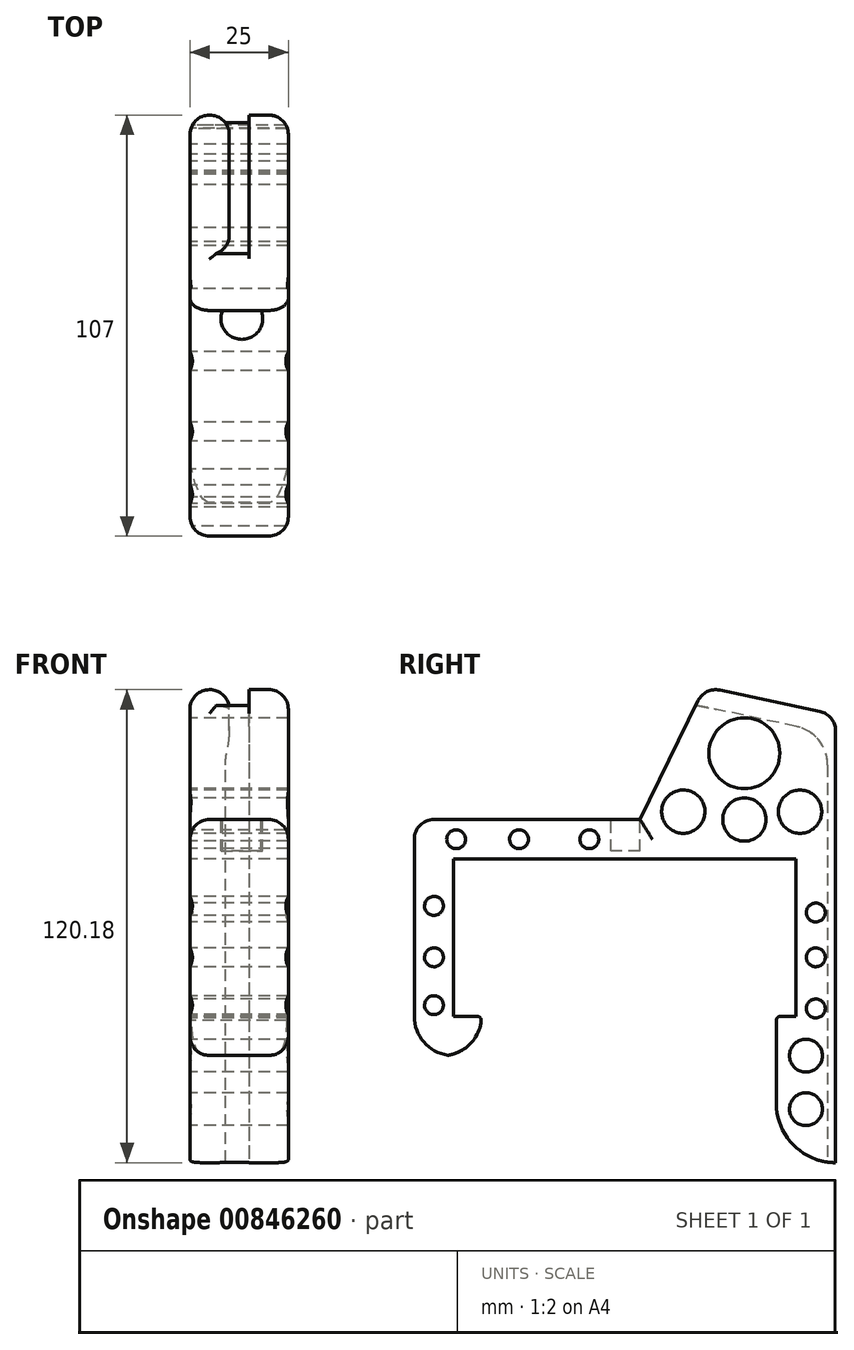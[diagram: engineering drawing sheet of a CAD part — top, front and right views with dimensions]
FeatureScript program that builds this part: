
annotation { "Feature Type Name" : "Feature", "Feature Type Description" : "" }
export const myFeature = defineFeature(function(context is Context, id is Id, definition is map)
    precondition{}
    {
        {
            var Q0;
            Q0=qCreatedBy(makeId("Right.planeOp"),FACE);
            var sketch = newSketch(context, id + "F0", { "sketchPlane" : qUnion([Q0])});
            skLineSegment(sketch, "E0.bottom", {"start": v(-21.63, 40) * mm, "end": v(65.37, 40) * mm, "construction": true});
            skLineSegment(sketch, "E0.top", {"start": v(-21.63, 0) * mm, "end": v(65.37, 0) * mm, "construction": true});
            skLineSegment(sketch, "E0.left", {"start": v(-21.63, 40) * mm, "end": v(-21.63, 0) * mm, "construction": true});
            skLineSegment(sketch, "E0.right", {"start": v(65.37, 40) * mm, "end": v(65.37, 0) * mm, "construction": true});
            skLineSegment(sketch, "E1.bottom", {"start": v(-31.63, 40) * mm, "end": v(75.37, 40) * mm});
            skLineSegment(sketch, "E1.top", {"start": v(-31.63, 50) * mm, "end": v(75.37, 50) * mm});
            skLineSegment(sketch, "E1.left", {"start": v(-31.63, 40) * mm, "end": v(-31.63, 50) * mm});
            skLineSegment(sketch, "E1.right", {"start": v(75.37, 40) * mm, "end": v(75.37, 50) * mm});
            skLineSegment(sketch, "E2.bottom", {"start": v(-31.63, 40) * mm, "end": v(-21.63, 40) * mm});
            skLineSegment(sketch, "E2.top", {"start": v(-31.63, 40) * mm, "end": v(-21.63, 40) * mm});
            skLineSegment(sketch, "E2.left", {"start": v(-31.63, 40) * mm, "end": v(-31.63, 40) * mm});
            skLineSegment(sketch, "E2.right", {"start": v(-21.63, 40) * mm, "end": v(-21.63, 40) * mm});
            skLineSegment(sketch, "E3.bottom", {"start": v(-21.63, 40) * mm, "end": v(-31.63, 40) * mm});
            skLineSegment(sketch, "E3.top", {"start": v(-21.63, -10) * mm, "end": v(-31.63, -10) * mm});
            skLineSegment(sketch, "E3.left", {"start": v(-21.63, 40) * mm, "end": v(-21.63, -10) * mm});
            skLineSegment(sketch, "E3.right", {"start": v(-31.63, 40) * mm, "end": v(-31.63, -10) * mm});
            skLineSegment(sketch, "E4.bottom", {"start": v(75.37, 40) * mm, "end": v(65.37, 40) * mm});
            skLineSegment(sketch, "E4.top", {"start": v(75.37, -10) * mm, "end": v(65.37, -10) * mm});
            skLineSegment(sketch, "E4.left", {"start": v(75.37, 40) * mm, "end": v(75.37, -10) * mm});
            skLineSegment(sketch, "E4.right", {"start": v(65.37, 40) * mm, "end": v(65.37, -10) * mm});
            skLineSegment(sketch, "E5.bottom", {"start": v(-21.63, -10) * mm, "end": v(-14.63, -10) * mm});
            skLineSegment(sketch, "E5.top", {"start": v(-21.63, 0) * mm, "end": v(-15.63, 0) * mm});
            skLineSegment(sketch, "E5.left", {"start": v(-21.63, -10) * mm, "end": v(-21.63, 0) * mm});
            skLineSegment(sketch, "E5.right", {"start": v(-14.63, -10) * mm, "end": v(-14.63, -1) * mm});
            skLineSegment(sketch, "E6.bottom", {"start": v(65.37, -10) * mm, "end": v(60.37, -10) * mm});
            skLineSegment(sketch, "E6.top", {"start": v(65.37, 0) * mm, "end": v(61.37, 0) * mm});
            skLineSegment(sketch, "E6.left", {"start": v(65.37, -10) * mm, "end": v(65.37, 0) * mm});
            skLineSegment(sketch, "E6.right", {"start": v(60.37, -10) * mm, "end": v(60.37, -1) * mm});
            skPoint(sketch, "E7.visualSharp", {"position": v(-14.63, 0) * mm});
            skArc(sketch, "E7.filletArc", {"start": v(-14.63, -1) * mm, "mid": v(-14.93, -0.3) * mm, "end": v(-15.63, 0) * mm});
            skPoint(sketch, "E8.visualSharp", {"position": v(60.37, 0) * mm});
            skArc(sketch, "E8.filletArc", {"start": v(61.37, 0) * mm, "mid": v(60.66, -0.3) * mm, "end": v(60.37, -1) * mm});
            skLineSegment(sketch, "E9.left", {"start": v(75.37, -10) * mm, "end": v(75.37, 0) * mm});
            skLineSegment(sketch, "E10.bottom", {"start": v(75.37, 50) * mm, "end": v(25.72, 50) * mm});
            skLineSegment(sketch, "E10.right", {"start": v(25.72, 50) * mm, "end": v(40.44, 80.2) * mm});
            skLineSegment(sketch, "E11.bottom", {"start": v(60.37, -10) * mm, "end": v(75.37, -10) * mm});
            skLineSegment(sketch, "E11.top", {"start": v(60.37, -37.18) * mm, "end": v(75.37, -37.18) * mm});
            skLineSegment(sketch, "E11.left", {"start": v(60.37, -10) * mm, "end": v(60.37, -37.18) * mm});
            skLineSegment(sketch, "E11.right", {"start": v(75.37, -10) * mm, "end": v(75.37, -37.18) * mm});
            skLineSegment(sketch, "E12", {"start": v(45.98, 82.9) * mm, "end": v(71.4, 77.49) * mm});
            skLineSegment(sketch, "E13", {"start": v(75.37, 72.6) * mm, "end": v(75.37, 50) * mm});
            skPoint(sketch, "E14.positionSnap0", {"position": v(58.76, 80.17) * mm});
            skPoint(sketch, "E14.positionSnap1", {"position": v(33.93, 66.85) * mm});
            skPoint(sketch, "E15", {"position": v(67.87, -23.6) * mm});
            skPoint(sketch, "E15.positionSnap0", {"position": v(75.37, -23.6) * mm});
            skPoint(sketch, "E15.positionSnap1", {"position": v(67.87, -10) * mm});
            skCircle(sketch, "E16", {"center": v(67.87, -23.6) * mm, "radius": 4.18 * mm});
            skPoint(sketch, "E17", {"position": v(70.37, 15) * mm});
            skPoint(sketch, "E17.positionSnap0", {"position": v(70.37, -10) * mm});
            skPoint(sketch, "E17.positionSnap1", {"position": v(65.37, 15) * mm});
            skPoint(sketch, "E18", {"position": v(-26.63, 15) * mm});
            skPoint(sketch, "E18.positionSnap0", {"position": v(-26.63, -10) * mm});
            skPoint(sketch, "E18.positionSnap1", {"position": v(-31.63, 15) * mm});
            skPoint(sketch, "E19", {"position": v(-26.63, 2.84) * mm});
            skPoint(sketch, "E20", {"position": v(-26.63, 28.06) * mm});
            skPoint(sketch, "E21", {"position": v(70.37, 2) * mm});
            skPoint(sketch, "E22", {"position": v(70.37, 26.38) * mm});
            skPoint(sketch, "E23", {"position": v(37.84, 45) * mm});
            skPoint(sketch, "E23.positionSnap0", {"position": v(75.37, 45) * mm});
            skPoint(sketch, "E24", {"position": v(12.84, 45) * mm});
            skPoint(sketch, "E25", {"position": v(-5.03, 45) * mm});
            skPoint(sketch, "E26", {"position": v(-21, 45) * mm});
            skCircle(sketch, "E27", {"center": v(70.37, 15) * mm, "radius": 2.4 * mm});
            skCircle(sketch, "E28", {"center": v(70.37, 2) * mm, "radius": 2.4 * mm});
            skCircle(sketch, "E29", {"center": v(70.37, 26.38) * mm, "radius": 2.4 * mm});
            skCircle(sketch, "E30", {"center": v(-26.63, 2.84) * mm, "radius": 2.4 * mm});
            skCircle(sketch, "E31", {"center": v(-26.63, 15) * mm, "radius": 2.4 * mm});
            skCircle(sketch, "E32", {"center": v(-26.63, 28.06) * mm, "radius": 2.4 * mm});
            skCircle(sketch, "E33", {"center": v(12.84, 45) * mm, "radius": 2.4 * mm});
            skCircle(sketch, "E34", {"center": v(-5.03, 45) * mm, "radius": 2.4 * mm});
            skCircle(sketch, "E35", {"center": v(-21, 45) * mm, "radius": 2.4 * mm});
            skCircle(sketch, "E36", {"center": v(67.87, -10) * mm, "radius": 4.18 * mm});
            skPoint(sketch, "E37", {"position": v(36.7, 52) * mm});
            skPoint(sketch, "E38", {"position": v(66.37, 52) * mm});
            skCircle(sketch, "E39", {"center": v(36.7, 52) * mm, "radius": 5.5 * mm});
            skCircle(sketch, "E40", {"center": v(66.37, 52) * mm, "radius": 5.5 * mm});
            skPoint(sketch, "E41.visualSharp", {"position": v(42.15, 83.7) * mm});
            skArc(sketch, "E41.filletArc", {"start": v(45.98, 82.9) * mm, "mid": v(42.74, 82.5) * mm, "end": v(40.44, 80.2) * mm});
            skPoint(sketch, "E42.visualSharp", {"position": v(75.37, 76.64) * mm});
            skArc(sketch, "E42.filletArc", {"start": v(75.37, 72.6) * mm, "mid": v(74.25, 75.74) * mm, "end": v(71.4, 77.49) * mm});
            skCircle(sketch, "E43", {"center": v(52.23, 66.85) * mm, "radius": 9 * mm});
            skCircle(sketch, "E44", {"center": v(52.23, 50) * mm, "radius": 5.5 * mm});
            skSolve(sketch);
        }
        {
            var Q0;
            Q0 = qSketchRegion(id + "F0", true);
            extrude(context, id + "F1", {"entities" : qUnion([Q0]), "depth" : 25 * mm, "offsetDistance" : 25 * mm});
        }
        {
            var Q0;
            Q0=makeQuery(id+"F1.opExtrude","SWEPT_EDGE",EDGE,{"disambiguationData":[OSD([sQuery(id+"F0.wireOp",EDGE,"E11.top"),sQuery(id+"F0.wireOp",EDGE,"E11.left")])]});
            fillet(context, id + "F2", {"entities" : qUnion([Q0]), "radius" : 15 * mm, "tangentPropagation" : true, "allowEdgeOverflow" : false});
        }
        {
            var Q0;
            Q0=makeQuery(id+"F1.opExtrude","SWEPT_EDGE",EDGE,{"disambiguationData":[OSD([sQuery(id+"F0.wireOp",EDGE,"E5.bottom"),sQuery(id+"F0.wireOp",EDGE,"E5.right")])]});
            var Q1;
            Q1=makeQuery(id+"F1.opExtrude","SWEPT_EDGE",EDGE,{"disambiguationData":[OSD([sQuery(id+"F0.wireOp",EDGE,"E3.top"),sQuery(id+"F0.wireOp",EDGE,"E3.right")])]});
            fillet(context, id + "F3", {"entities" : qUnion([Q0, Q1]), "radius" : 10 * mm, "tangentPropagation" : true, "allowEdgeOverflow" : false});
        }
        {
            var Q0;
            Q0=makeQuery(id+"F1.opExtrude","SWEPT_FACE",FACE,{"disambiguationData":[OSD([sQuery(id+"F0.wireOp",EDGE,"E12")])]});
            var sketch = newSketch(context, id + "F4", { "sketchPlane" : qUnion([Q0])});
            skLineSegment(sketch, "E45.bottom", {"start": v(10, 58.63) * mm, "end": v(15, 58.63) * mm});
            skLineSegment(sketch, "E45.top", {"start": v(10, 22.88) * mm, "end": v(15, 22.88) * mm});
            skLineSegment(sketch, "E45.left", {"start": v(10, 58.63) * mm, "end": v(10, 22.88) * mm});
            skLineSegment(sketch, "E45.right", {"start": v(15, 58.63) * mm, "end": v(15, 22.88) * mm});
            skSolve(sketch);
        }
        {
            var Q0;
            {var subQ0=sQuery(id+"F4.wireOp",EDGE,"E45.bottom");Q0=makeQuery(id+"F4.imprint","IMPRINT",FACE,{"disambiguationData":[TD([[makeQuery(id+"F4.imprint","IMPRINT",EDGE,{"derivedFrom":subQ0}),-1.0]])]});}
            var Q1;
            {var subQ0=sQuery(id+"F4.wireOp",EDGE,"E45.left");var subQ1=sQuery(id+"F0.wireOp",EDGE,"E12");var subQ2=makeQuery(id+"F1.opExtrude","SWEPT_EDGE",EDGE,{"disambiguationData":[OSD([subQ1,sQuery(id+"F0.wireOp",EDGE,"E42.filletArc")])]});var subQ3=makeQuery(id+"F4.imprint","INTERSECT",VERTEX,{"derivedFrom":[subQ2,subQ0]});Q1=makeQuery(id+"F4.imprint","IMPRINT",FACE,{"disambiguationData":[TD([[makeQuery(id+"F4.imprint","IMPRINT",EDGE,{"disambiguationData":[TD([[subQ3,-1.0]])],"derivedFrom":subQ0}),1.0]])]});}
            var Q2;
            {var subQ0=sQuery(id+"F4.wireOp",EDGE,"E45.top");Q2=makeQuery(id+"F4.imprint","IMPRINT",FACE,{"disambiguationData":[TD([[makeQuery(id+"F4.imprint","IMPRINT",EDGE,{"derivedFrom":subQ0}),1.0]])]});}
            extrude(context, id + "F5", {"entities" : qUnion([Q0, Q1, Q2]), "operationType" : NewBodyOperationType.REMOVE, "oppositeDirection" : true, "depth" : 5 * mm, "offsetDistance" : 25 * mm});
        }
        {
            var Q0;
            Q0=makeQuery(id+"F1.opExtrude","SWEPT_FACE",FACE,{"disambiguationData":[OSD([sQuery(id+"F0.wireOp",EDGE,"E1.right"),sQuery(id+"F0.wireOp",EDGE,"E4.left"),sQuery(id+"F0.wireOp",EDGE,"E9.left"),sQuery(id+"F0.wireOp",EDGE,"E11.right"),sQuery(id+"F0.wireOp",EDGE,"E13")])]});
            var sketch = newSketch(context, id + "F6", { "sketchPlane" : qUnion([Q0])});
            skLineSegment(sketch, "E46.bottom", {"start": v(-15, 72.6) * mm, "end": v(-10, 72.6) * mm});
            skLineSegment(sketch, "E46.top", {"start": v(-15, -37.18) * mm, "end": v(-10, -37.18) * mm});
            skLineSegment(sketch, "E46.left", {"start": v(-15, 72.6) * mm, "end": v(-15, -37.18) * mm});
            skLineSegment(sketch, "E46.right", {"start": v(-10, 72.6) * mm, "end": v(-10, -37.18) * mm});
            skSolve(sketch);
        }
        {
            var Q0;
            Q0 = qSketchRegion(id + "F6", true);
            extrude(context, id + "F7", {"entities" : qUnion([Q0]), "operationType" : NewBodyOperationType.REMOVE, "oppositeDirection" : true, "depth" : 2 * mm, "offsetDistance" : 25 * mm});
        }
        {
            var Q0;
            {var subQ0=sQuery(id+"F4.wireOp",EDGE,"E45.bottom");var subQ1=sQuery(id+"F4.wireOp",EDGE,"E45.right");var subQ2=sQuery(id+"F4.wireOp",EDGE,"E45.left");Q0=makeQuery(id+"F7.boolean.opBoolean","INTERSECT",EDGE,{"derivedFrom":[makeQuery(id+"F5.boolean.opBoolean","COPY",FACE,{"disambiguationData":[TD([makeQuery(id+"F5.opExtrude","SWEPT_FACE",FACE,{"disambiguationData":[OSD([subQ0])]})])],"derivedFrom":makeQuery(id+"F5.opExtrude","CAP_FACE",FACE,{"disambiguationData":[OSD([subQ0,sQuery(id+"F4.wireOp",EDGE,"E45.top"),subQ2,subQ1])],"isStart":false})}),makeQuery(id+"F7.opExtrude","CAP_FACE",FACE,{"disambiguationData":[OSD([sQuery(id+"F6.wireOp",EDGE,"E46.bottom"),sQuery(id+"F6.wireOp",EDGE,"E46.top"),sQuery(id+"F6.wireOp",EDGE,"E46.left"),sQuery(id+"F6.wireOp",EDGE,"E46.right")])],"isStart":false})]});}
            var Q1;
            {var subQ0=sQuery(id+"F0.wireOp",EDGE,"E10.right");Q1=makeQuery(id+"F5.boolean.opBoolean","SPLIT",EDGE,{"disambiguationData":[topologyDisambiguationEdgeConnected([makeQuery(id+"F1.opExtrude","SWEPT_FACE",FACE,{"disambiguationData":[OSD([subQ0])]}),makeQuery(id+"F5.opExtrude","SWEPT_FACE",FACE,{"disambiguationData":[OSD([sQuery(id+"F4.wireOp",EDGE,"E45.top")])]})])],"derivedFrom":makeQuery(id+"F1.opExtrude","SWEPT_EDGE",EDGE,{"disambiguationData":[OSD([subQ0,sQuery(id+"F0.wireOp",EDGE,"E41.filletArc")])]})});}
            fillet(context, id + "F8", {"entities" : qUnion([Q0, Q1]), "radius" : 10 * mm, "tangentPropagation" : true, "allowEdgeOverflow" : false});
        }
        {
            var Q0;
            Q0=makeQuery(id+"F7.boolean.opBoolean","COPY",EDGE,{"derivedFrom":makeQuery(id+"F7.opExtrude","CAP_EDGE",EDGE,{"disambiguationData":[OSD([sQuery(id+"F6.wireOp",EDGE,"E46.left")])],"isStart":true})});
            var Q1;
            Q1=makeQuery(id+"F7.boolean.opBoolean","COPY",EDGE,{"derivedFrom":makeQuery(id+"F7.opExtrude","CAP_EDGE",EDGE,{"disambiguationData":[OSD([sQuery(id+"F6.wireOp",EDGE,"E46.right")])],"isStart":true})});
            fillet(context, id + "F9", {"entities" : qUnion([Q0, Q1]), "radius" : 5 * mm, "tangentPropagation" : true, "allowEdgeOverflow" : false});
        }
        {
            var Q0;
            Q0=makeQuery(id+"F1.opExtrude","CAP_EDGE",EDGE,{"disambiguationData":[OSD([sQuery(id+"F0.wireOp",EDGE,"E10.right")])],"isStart":false});
            var Q1;
            Q1=makeQuery(id+"F1.opExtrude","CAP_EDGE",EDGE,{"disambiguationData":[OSD([sQuery(id+"F0.wireOp",EDGE,"E10.right")])],"isStart":true});
            var Q2;
            Q2=makeQuery(id+"F1.opExtrude","CAP_EDGE",EDGE,{"disambiguationData":[OSD([sQuery(id+"F0.wireOp",EDGE,"E1.top")])],"isStart":false});
            var Q3;
            Q3=makeQuery(id+"F1.opExtrude","CAP_EDGE",EDGE,{"disambiguationData":[OSD([sQuery(id+"F0.wireOp",EDGE,"E1.top")])],"isStart":true});
            var Q4;
            Q4=makeQuery(id+"F1.opExtrude","SWEPT_EDGE",EDGE,{"disambiguationData":[OSD([sQuery(id+"F0.wireOp",EDGE,"E1.top"),sQuery(id+"F0.wireOp",EDGE,"E1.left")])]});
            var Q5;
            Q5=makeQuery(id+"F1.opExtrude","CAP_EDGE",EDGE,{"disambiguationData":[OSD([sQuery(id+"F0.wireOp",EDGE,"E1.left"),sQuery(id+"F0.wireOp",EDGE,"E3.right")])],"isStart":false});
            var Q6;
            Q6=makeQuery(id+"F1.opExtrude","CAP_EDGE",EDGE,{"disambiguationData":[OSD([sQuery(id+"F0.wireOp",EDGE,"E1.left"),sQuery(id+"F0.wireOp",EDGE,"E3.right")])],"isStart":true});
            fillet(context, id + "F10", {"entities" : qUnion([Q0, Q1, Q2, Q3, Q4, Q5, Q6]), "radius" : 5 * mm, "tangentPropagation" : true, "allowEdgeOverflow" : false});
        }
        {
            var Q0;
            Q0=makeQuery(id+"F1.opExtrude","SWEPT_FACE",FACE,{"disambiguationData":[OSD([sQuery(id+"F0.wireOp",EDGE,"E1.top")])]});
            var sketch = newSketch(context, id + "F11", { "sketchPlane" : qUnion([Q0])});
            skArc(sketch, "E47", {"start": v(8.27, 25.72) * mm, "mid": v(13.19, 18.36) * mm, "end": v(18.1, 25.72) * mm});
            skSolve(sketch);
        }
        {
            var Q0;
            Q0 = qSketchRegion(id + "F11", true);
            var Q1;
            {var subQ0=sQuery(id+"F11.wireOp",EDGE,"E47");Q1=makeQuery(id+"F11.imprint","IMPRINT",FACE,{"disambiguationData":[TD([[makeQuery(id+"F11.imprint","IMPRINT",EDGE,{"derivedFrom":subQ0}),1.0]])]});}
            extrude(context, id + "F12", {"entities" : qUnion([Q0, Q1]), "operationType" : NewBodyOperationType.REMOVE, "oppositeDirection" : true, "depth" : 8 * mm, "offsetDistance" : 25 * mm});
        }
    });
